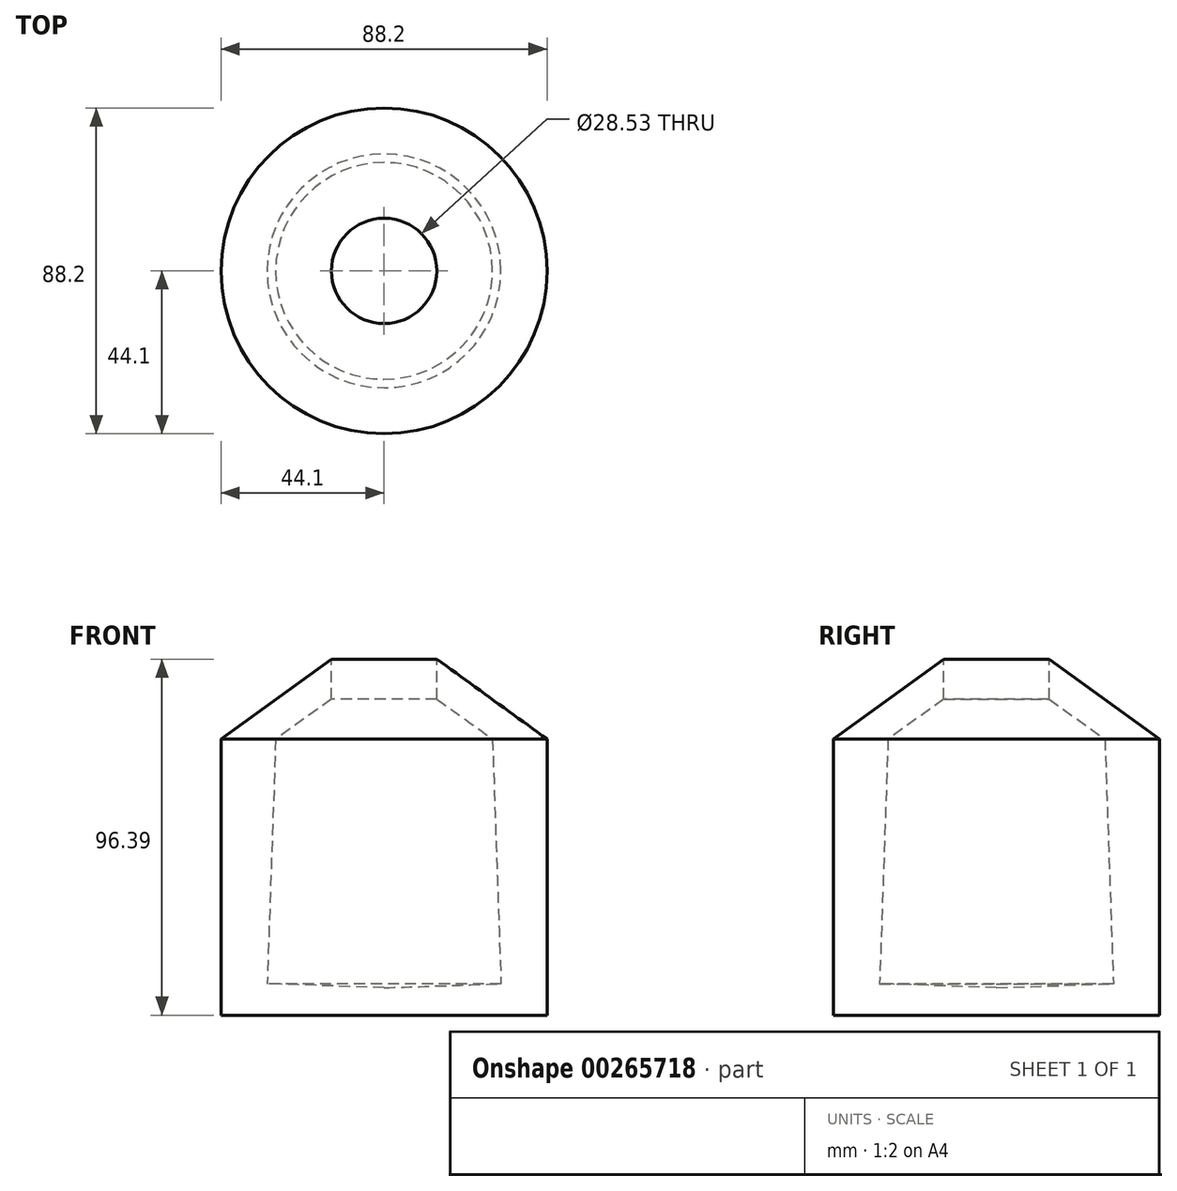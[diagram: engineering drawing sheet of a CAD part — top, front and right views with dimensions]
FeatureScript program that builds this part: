
annotation { "Feature Type Name" : "Feature", "Feature Type Description" : "" }
export const myFeature = defineFeature(function(context is Context, id is Id, definition is map)
    precondition{}
    {
        {
            var Q0;
            Q0=qCreatedBy(makeId("Front.planeOp"),FACE);
            var sketch = newSketch(context, id + "F0", { "sketchPlane" : qUnion([Q0])});
            skLineSegment(sketch, "E0", {"start": v(0, -53.77) * mm, "end": v(44.1, -53.77) * mm});
            skLineSegment(sketch, "E1", {"start": v(44.1, -53.77) * mm, "end": v(44.1, 20.98) * mm});
            skLineSegment(sketch, "E2", {"start": v(44.1, 20.98) * mm, "end": v(14.26, 42.62) * mm});
            skLineSegment(sketch, "E3", {"start": v(14.26, 42.62) * mm, "end": v(14.26, 31.8) * mm});
            skLineSegment(sketch, "E4", {"start": v(14.26, 31.8) * mm, "end": v(29.35, 20.98) * mm});
            skLineSegment(sketch, "E5", {"start": v(29.35, 20.98) * mm, "end": v(31.64, -45.25) * mm});
            skLineSegment(sketch, "E6", {"start": v(31.64, -45.25) * mm, "end": v(0, -46.34) * mm});
            skLineSegment(sketch, "E7", {"start": v(0, -46.34) * mm, "end": v(0, -53.77) * mm});
            skSolve(sketch);
        }
        {
            var Q0;
            Q0=makeQuery(id+"F0.imprint","IMPRINT",FACE,{"disambiguationData":[TD([[makeQuery(id+"F0.imprint","IMPRINT",EDGE,{"derivedFrom":sQuery(id+"F0.wireOp",EDGE,"E0")}),1.0]])]});
            var Q1;
            Q1=sQuery(id+"F0.wireOp",EDGE,"E7");
            revolve(context, id + "F1", {"entities" : qUnion([Q0]), "axis" : qUnion([Q1]), "revolveType" : RevolveType.FULL});
        }
    });
